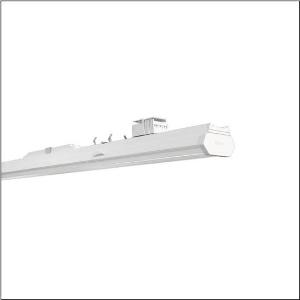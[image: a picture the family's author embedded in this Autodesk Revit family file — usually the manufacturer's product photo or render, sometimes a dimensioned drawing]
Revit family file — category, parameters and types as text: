
# Revit family: licross_r__21_protected_mo_52td12cn675f_4ad1
name_source: partatom
category: Lighting Fixtures
units: mm (PartAtom-declared; Revit-internal decimal feet)

## family parameters
Cut with Voids When Loaded = No
Host = Face
Light Source = No
Part Type = Normal
Room Calculation Point = No
Round Connector Dimension = Use Diameter
Shared = No

## types (1)
- --- (1 x LED, 7960 lm, 48.5 W, 6500K)
    Apparent Load = 49 VA
    CIE Flux Codes = 73 92 98 99 100
    Color Rendering = 80
    Color Temperature = 6500K
    Default Elevation = 1800 mm
    Description = Licross® 21 Protected MO, luminaire insert, of sheet steel, galvanised, coil coated, white, length: 1.500mm, width: 90mm, height: 101mm, LED rated luminous flux: 7.940lm, light colour: 865, control gear: ON/OFF Multilumen, CLOi, control gear: ECG Multilumen, with plug, 3-pole, with phase selection, mains connection: 220..240V, AC, 50/60Hz, start of lifetime: 49W, end of service life: 55W, halogen-free wiring, primary optical cover: cover, of PMMA, light emission: direct distribution, primary light characteristic: symmetric, protection rating (complete): IP54, insulation class (complete): insulation class I (protective earthing), certification: CE, ENEC, VDE, UKCA, protection symbol: D if used in an environment with non-conductive dust loads with corresponding accessories, impact resistance: IK06, permissible ambient temperature for indoor applications: -35..+45°C, corresponds to IFS (International Featured Standards) requirements for safety and quality in the food industry, reducing of maximum allowable ambient temperature of 5°C with ceiling mounting, LABS conformity tested according to VDMA 24364:2018-05, packaging unit: 1 piece
    Height = 92 mm
    Lamp = 1 x LED
    Lamp Light Flux = 7960 lm
    Lamp Power = 48.5 W
    Lamp count = 1
    Length = 1500 mm
    Luminous efficacy = 164 lm/W
    Manufacturer = Siteco
    ModVariant = No
    Model = 52TD12CN675F
    Mounting Place = Ceiling
    Mounting Type = Pendant
    Number of Poles = 1
    OnlyDefault = Yes
    Power Factor = 1
    Product Name = Licross® 21 Protected MO
    Product group = luminaire insert
    ProductGroupID = 901
    Protection Class = Protection class I
    Protection Degree = IP 54
    RLX_Detail_Level = 1
    RLX_Emergency_Light_Flux = 0 lm
    RLX_Emergency_Type = 0
    RLX_Emergency_Type_DB = No
    RlxData = <blob elided: 22065 chars, md5=39fe7493>
    Socket = socket
    Standby Power = 0 W
    System Light Flux = 7960 lm
    System Power = 49 W
    Type Comments = factory setting: luminous flux: 100 % | (A | C | E) | 117 mA
    Type Image = l_1256148.jpg
    URL = http://relux.com
    VarID = @adj_149633
    Voltage = 0 V
    Weight = 0.00 kg
    Width = 88 mm

## geometry (parser evidence)
native form markers: Blend x4, Sweep x10
no freeform markers — native parametric forms only
